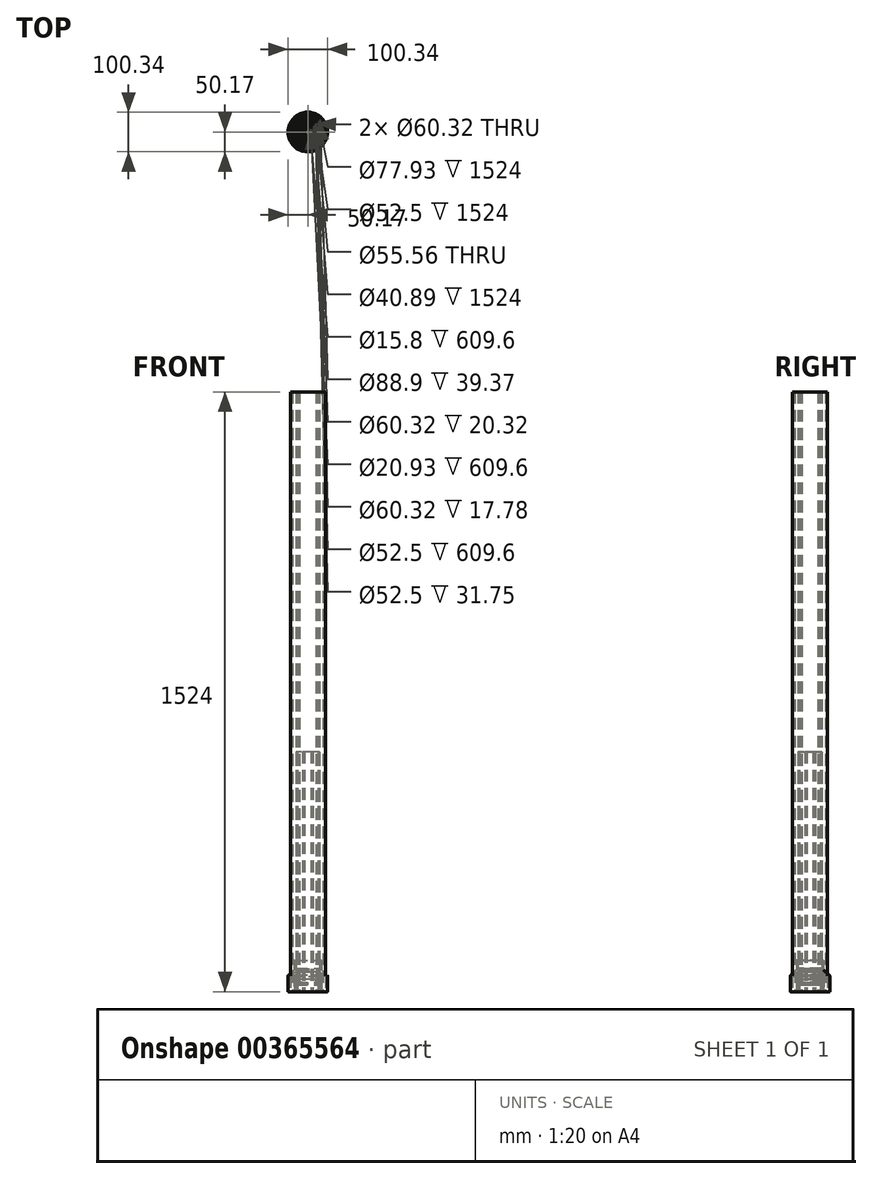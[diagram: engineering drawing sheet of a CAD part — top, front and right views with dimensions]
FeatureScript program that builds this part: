
annotation { "Feature Type Name" : "Feature", "Feature Type Description" : "" }
export const myFeature = defineFeature(function(context is Context, id is Id, definition is map)
    precondition{}
    {
        {
            var Q0;
            Q0=qCreatedBy(makeId("Top.planeOp"),FACE);
            var sketch = newSketch(context, id + "F0", { "sketchPlane" : qUnion([Q0])});
            skCircle(sketch, "E0", {"center": v(0, 0) * mm, "radius": 20.45 * mm});
            skCircle(sketch, "E1", {"center": v(0, 0) * mm, "radius": 24.13 * mm});
            skSolve(sketch);
        }
        {
            var Q0;
            Q0=makeQuery(id+"F0.imprint","IMPRINT",FACE,{"disambiguationData":[TD([[makeQuery(id+"F0.imprint","IMPRINT",EDGE,{"derivedFrom":sQuery(id+"F0.wireOp",EDGE,"E0")}),-1.0]])]});
            extrude(context, id + "F1", {"entities" : qUnion([Q0]), "depth" : 1524 * mm});
        }
        {
            var Q0;
            Q0=qCreatedBy(makeId("Top.planeOp"),FACE);
            var sketch = newSketch(context, id + "F2", { "sketchPlane" : qUnion([Q0])});
            skCircle(sketch, "E2", {"center": v(0, 0) * mm, "radius": 26.25 * mm});
            skCircle(sketch, "E3", {"center": v(0, 0) * mm, "radius": 30.16 * mm});
            skSolve(sketch);
        }
        {
            var Q0;
            Q0 = qSketchRegion(id + "F2", true);
            extrude(context, id + "F3", {"entities" : qUnion([Q0]), "depth" : 1524 * mm});
        }
        {
            var Q0;
            Q0=qCreatedBy(makeId("Top.planeOp"),FACE);
            var sketch = newSketch(context, id + "F4", { "sketchPlane" : qUnion([Q0])});
            skCircle(sketch, "E4", {"center": v(0, 0) * mm, "radius": 38.96 * mm});
            skCircle(sketch, "E5", {"center": v(0, 0) * mm, "radius": 44.45 * mm});
            skSolve(sketch);
        }
        {
            var Q0;
            Q0 = qSketchRegion(id + "F4", true);
            extrude(context, id + "F5", {"entities" : qUnion([Q0]), "depth" : 1524 * mm});
        }
        {
            var Q0;
            Q0=qCreatedBy(makeId("Right.planeOp"),FACE);
            var sketch = newSketch(context, id + "F6", { "sketchPlane" : qUnion([Q0])});
            skLineSegment(sketch, "E6", {"start": v(0, 0) * mm, "end": v(0, 95.28) * mm, "construction": true});
            skLineSegment(sketch, "E7", {"start": v(24.13, 50.8) * mm, "end": v(24.13, 33.02) * mm});
            skLineSegment(sketch, "E8", {"start": v(24.13, 33.02) * mm, "end": v(19.05, 26.67) * mm});
            skLineSegment(sketch, "E9", {"start": v(19.05, 26.67) * mm, "end": v(19.05, 24.13) * mm});
            skLineSegment(sketch, "E10", {"start": v(19.05, 24.13) * mm, "end": v(30.16, 17.78) * mm});
            skLineSegment(sketch, "E11", {"start": v(30.16, 17.78) * mm, "end": v(30.16, 0) * mm});
            skLineSegment(sketch, "E12", {"start": v(30.16, 0) * mm, "end": v(34.3, 0) * mm});
            skLineSegment(sketch, "E13", {"start": v(34.3, 0) * mm, "end": v(34.3, 20.64) * mm});
            skLineSegment(sketch, "E14", {"start": v(34.3, 20.64) * mm, "end": v(28.45, 26.99) * mm});
            skLineSegment(sketch, "E15", {"start": v(28.45, 26.99) * mm, "end": v(28.45, 50.8) * mm});
            skLineSegment(sketch, "E16", {"start": v(28.45, 50.8) * mm, "end": v(24.13, 50.8) * mm});
            skSolve(sketch);
        }
        {
            var Q0;
            Q0 = qSketchRegion(id + "F6", true);
            var Q1;
            Q1=sQuery(id+"F6.wireOp",EDGE,"E6");
            revolve(context, id + "F7", {"entities" : qUnion([Q0]), "axis" : qUnion([Q1]), "revolveType" : RevolveType.FULL});
        }
        {
            var Q0;
            Q0=makeQuery(id+"F7.opRevolve","SWEPT_EDGE",EDGE,{"disambiguationData":[OSD([sQuery(id+"F6.wireOp",EDGE,"E15"),sQuery(id+"F6.wireOp",EDGE,"E16")])]});
            var Q1;
            Q1=makeQuery(id+"F7.opRevolve","SWEPT_EDGE",EDGE,{"disambiguationData":[OSD([sQuery(id+"F6.wireOp",EDGE,"E14"),sQuery(id+"F6.wireOp",EDGE,"E15")])]});
            var Q2;
            Q2=makeQuery(id+"F7.opRevolve","SWEPT_EDGE",EDGE,{"disambiguationData":[OSD([sQuery(id+"F6.wireOp",EDGE,"E13"),sQuery(id+"F6.wireOp",EDGE,"E14")])]});
            var Q3;
            Q3=makeQuery(id+"F7.opRevolve","SWEPT_EDGE",EDGE,{"disambiguationData":[OSD([sQuery(id+"F6.wireOp",EDGE,"E9"),sQuery(id+"F6.wireOp",EDGE,"E10")])]});
            var Q4;
            Q4=makeQuery(id+"F7.opRevolve","SWEPT_EDGE",EDGE,{"disambiguationData":[OSD([sQuery(id+"F6.wireOp",EDGE,"E8"),sQuery(id+"F6.wireOp",EDGE,"E9")])]});
            fillet(context, id + "F8", {"entities" : qUnion([Q0, Q1, Q2, Q3, Q4]), "radius" : 0.4 * mm, "tangentPropagation" : true, "allowEdgeOverflow" : false});
        }
        {
            var Q0;
            Q0=qCreatedBy(makeId("Right.planeOp"),FACE);
            var sketch = newSketch(context, id + "F9", { "sketchPlane" : qUnion([Q0])});
            skLineSegment(sketch, "E17", {"start": v(0, 0) * mm, "end": v(0, 103.87) * mm, "construction": true});
            skLineSegment(sketch, "E18", {"start": v(44.45, 0) * mm, "end": v(44.45, 39.37) * mm});
            skLineSegment(sketch, "E19", {"start": v(44.45, 39.37) * mm, "end": v(25.4, 54.61) * mm});
            skLineSegment(sketch, "E20", {"start": v(25.4, 54.61) * mm, "end": v(25.4, 57.79) * mm});
            skLineSegment(sketch, "E21", {"start": v(25.4, 57.79) * mm, "end": v(30.16, 59.05) * mm});
            skLineSegment(sketch, "E22", {"start": v(30.16, 59.05) * mm, "end": v(30.16, 79.38) * mm});
            skLineSegment(sketch, "E23", {"start": v(30.16, 79.38) * mm, "end": v(34.54, 79.38) * mm});
            skLineSegment(sketch, "E24", {"start": v(34.54, 79.38) * mm, "end": v(34.54, 55.25) * mm});
            skLineSegment(sketch, "E25", {"start": v(34.54, 55.25) * mm, "end": v(50.17, 40.64) * mm});
            skLineSegment(sketch, "E26", {"start": v(50.17, 40.64) * mm, "end": v(50.17, 0) * mm});
            skLineSegment(sketch, "E27", {"start": v(50.17, 0) * mm, "end": v(44.45, 0) * mm});
            skSolve(sketch);
        }
        {
            var Q0;
            Q0 = qSketchRegion(id + "F9", true);
            var Q1;
            Q1=sQuery(id+"F9.wireOp",EDGE,"E17");
            revolve(context, id + "F10", {"entities" : qUnion([Q0]), "axis" : qUnion([Q1]), "revolveType" : RevolveType.FULL});
        }
        {
            var Q0;
            Q0=makeQuery(id+"F10.opRevolve","SWEPT_EDGE",EDGE,{"disambiguationData":[OSD([sQuery(id+"F9.wireOp",EDGE,"E26"),sQuery(id+"F9.wireOp",EDGE,"E27")])]});
            var Q1;
            Q1=makeQuery(id+"F10.opRevolve","SWEPT_EDGE",EDGE,{"disambiguationData":[OSD([sQuery(id+"F9.wireOp",EDGE,"E25"),sQuery(id+"F9.wireOp",EDGE,"E26")])]});
            var Q2;
            Q2=makeQuery(id+"F10.opRevolve","SWEPT_EDGE",EDGE,{"disambiguationData":[OSD([sQuery(id+"F9.wireOp",EDGE,"E24"),sQuery(id+"F9.wireOp",EDGE,"E25")])]});
            var Q3;
            Q3=makeQuery(id+"F10.opRevolve","SWEPT_EDGE",EDGE,{"disambiguationData":[OSD([sQuery(id+"F9.wireOp",EDGE,"E23"),sQuery(id+"F9.wireOp",EDGE,"E24")])]});
            fillet(context, id + "F11", {"entities" : qUnion([Q0, Q1, Q2, Q3]), "radius" : 0.4 * mm, "tangentPropagation" : true, "allowEdgeOverflow" : false});
        }
        {
            var Q0;
            Q0=qCreatedBy(makeId("Right.planeOp"),FACE);
            var sketch = newSketch(context, id + "F12", { "sketchPlane" : qUnion([Q0])});
            skLineSegment(sketch, "E28", {"start": v(0, 0) * mm, "end": v(0, 46.8) * mm, "construction": true});
            skLineSegment(sketch, "E29", {"start": v(34.93, 42.86) * mm, "end": v(34.93, 0) * mm});
            skLineSegment(sketch, "E30", {"start": v(34.93, 0) * mm, "end": v(30.16, 0) * mm});
            skLineSegment(sketch, "E31", {"start": v(30.16, 0) * mm, "end": v(30.16, 19.05) * mm});
            skLineSegment(sketch, "E32", {"start": v(30.16, 19.05) * mm, "end": v(27.78, 20.16) * mm});
            skLineSegment(sketch, "E33", {"start": v(27.78, 20.16) * mm, "end": v(27.78, 22.7) * mm});
            skLineSegment(sketch, "E34", {"start": v(27.78, 22.7) * mm, "end": v(30.16, 23.81) * mm});
            skLineSegment(sketch, "E35", {"start": v(30.16, 23.81) * mm, "end": v(30.16, 42.86) * mm});
            skLineSegment(sketch, "E36", {"start": v(30.16, 42.86) * mm, "end": v(34.93, 42.86) * mm});
            skLineSegment(sketch, "E37", {"start": v(34.93, 21.43) * mm, "end": v(27.78, 21.43) * mm, "construction": true});
            skSolve(sketch);
        }
        {
            var Q0;
            Q0 = qSketchRegion(id + "F12", true);
            var Q1;
            Q1=sQuery(id+"F12.wireOp",EDGE,"E28");
            revolve(context, id + "F13", {"entities" : qUnion([Q0]), "axis" : qUnion([Q1]), "revolveType" : RevolveType.FULL});
        }
        {
            var Q0;
            Q0=makeQuery(id+"F13.opRevolve","SWEPT_EDGE",EDGE,{"disambiguationData":[OSD([sQuery(id+"F12.wireOp",EDGE,"E35"),sQuery(id+"F12.wireOp",EDGE,"E36")])]});
            var Q1;
            Q1=makeQuery(id+"F13.opRevolve","SWEPT_EDGE",EDGE,{"disambiguationData":[OSD([sQuery(id+"F12.wireOp",EDGE,"E29"),sQuery(id+"F12.wireOp",EDGE,"E36")])]});
            var Q2;
            Q2=makeQuery(id+"F13.opRevolve","SWEPT_EDGE",EDGE,{"disambiguationData":[OSD([sQuery(id+"F12.wireOp",EDGE,"E29"),sQuery(id+"F12.wireOp",EDGE,"E30")])]});
            var Q3;
            Q3=makeQuery(id+"F13.opRevolve","SWEPT_EDGE",EDGE,{"disambiguationData":[OSD([sQuery(id+"F12.wireOp",EDGE,"E30"),sQuery(id+"F12.wireOp",EDGE,"E31")])]});
            fillet(context, id + "F14", {"entities" : qUnion([Q0, Q1, Q2, Q3]), "radius" : 0.4 * mm, "tangentPropagation" : true, "allowEdgeOverflow" : false});
        }
        {
            var Q0;
            Q0 = qSketchRegion(id + "F2", true);
            extrude(context, id + "F15", {"entities" : qUnion([Q0]), "depth" : 609.6 * mm});
        }
        {
            var Q0;
            Q0 = qSketchRegion(id + "F2", true);
            extrude(context, id + "F16", {"entities" : qUnion([Q0]), "depth" : 31.75 * mm});
        }
        {
            var Q0;
            Q0=qCreatedBy(makeId("Top.planeOp"), FACE);
            var sketch = newSketch(context, id + "F17", { "sketchPlane" : qUnion([Q0])});
            skCircle(sketch, "E38", {"center": v(0, 0) * mm, "radius": 13.34 * mm});
            skCircle(sketch, "E39", {"center": v(0, 0) * mm, "radius": 10.46 * mm});
            skSolve(sketch);
        }
        {
            var Q0;
            Q0 = qSketchRegion(id + "F17", true);
            extrude(context, id + "F18", {"entities" : qUnion([Q0]), "domain" : OperationDomain.MODEL, "flatOperationType" : FlatOperationType.REMOVE, "depth" : 609.6 * mm, "offsetDistance" : 25 * mm});
        }
        {
            var Q0;
            Q0=qCreatedBy(makeId("Top.planeOp"), FACE);
            var sketch = newSketch(context, id + "F19", { "sketchPlane" : qUnion([Q0])});
            skCircle(sketch, "E40", {"center": v(0, 0) * mm, "radius": 10.67 * mm});
            skCircle(sketch, "E41", {"center": v(0, 0) * mm, "radius": 7.9 * mm});
            skSolve(sketch);
        }
        {
            var Q0;
            Q0 = qSketchRegion(id + "F19", true);
            extrude(context, id + "F20", {"entities" : qUnion([Q0]), "domain" : OperationDomain.MODEL, "flatOperationType" : FlatOperationType.REMOVE, "depth" : 609.6 * mm, "offsetDistance" : 25 * mm});
        }
    });
